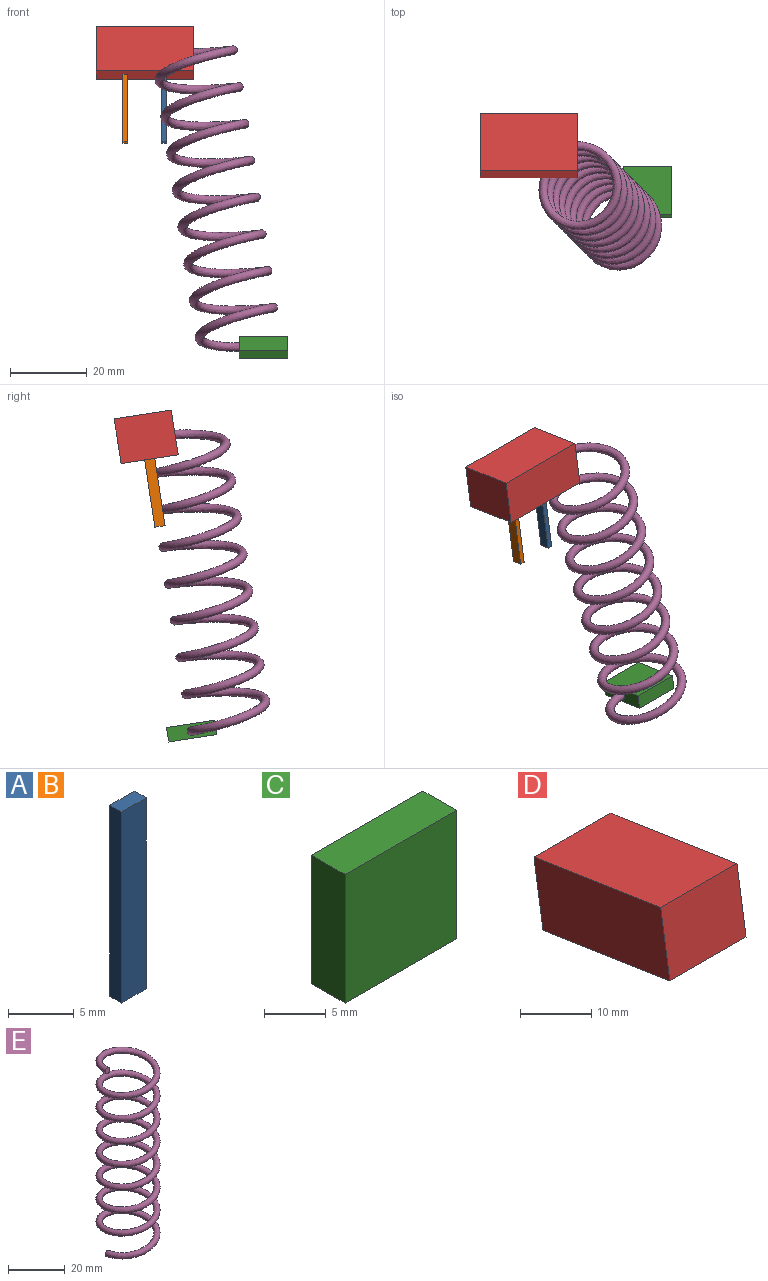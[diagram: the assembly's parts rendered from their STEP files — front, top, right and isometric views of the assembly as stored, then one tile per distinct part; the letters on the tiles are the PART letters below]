
ASSEMBLY  parts=5 mates=4
PART A: 6 faces, bbox 2.7x1.3x17.8 mm
  f0: plane 17.78x1.27mm, normal (-1,0,0), area 22.6mm2, adj f1,f3,f4,f5
  f1: plane 2.68x1.27mm, normal (0,0,-1), area 3.4mm2, adj f0,f2,f4,f5
  f2: plane 17.78x1.27mm, normal (1,0,0), area 22.6mm2, adj f1,f3,f4,f5
  f3: plane 2.68x1.27mm, normal (0,0,1), area 3.4mm2, adj f0,f2,f4,f5
  f4: plane 17.78x2.68mm, normal (0,-1,0), area 47.6mm2, adj f0,f1,f2,f3
  f5: plane 17.78x2.68mm, normal (0,1,0), area 47.6mm2, adj f0,f1,f2,f3
PART B: same geometry as A
PART C: 6 faces, bbox 12.7x3.8x12.7 mm
  f0: plane 12.7x3.81mm, normal (-1,0,0), area 48.4mm2, adj f1,f3,f4,f5
  f1: plane 12.7x12.7mm, normal (0,-1,0), area 161.3mm2, adj f0,f2,f4,f5
  f2: plane 12.7x3.81mm, normal (1,0,0), area 48.4mm2, adj f1,f3,f4,f5
  f3: plane 12.7x12.7mm, normal (0,1,0), area 161.3mm2, adj f0,f2,f4,f5
  f4: plane 12.7x3.81mm, normal (0,0,1), area 48.4mm2, adj f0,f1,f2,f3
  f5: plane 12.7x3.81mm, normal (0,0,-1), area 48.4mm2, adj f0,f1,f2,f3
PART D: 6 faces, bbox 15.1x26.9x15.6 mm
  f0: plane 26.91x15.56mm, normal (1,0,0), area 300.4mm2, adj f2,f3,f4,f5
  f1: plane 26.91x15.56mm, normal (-1,0,0), area 300.4mm2, adj f2,f3,f4,f5
  f2: plane 25.1x15.09mm, normal (0,0.15,0.99), area 383.2mm2, adj f0,f1,f3,f4
  f3: plane 15.09x11.69mm, normal (0,0.99,-0.15), area 178.4mm2, adj f0,f1,f2,f5
  f4: plane 15.09x11.69mm, normal (0,-0.99,0.15), area 178.4mm2, adj f0,f1,f2,f5
  f5: plane 25.1x15.09mm, normal (0,-0.15,-0.99), area 383.2mm2, adj f0,f1,f3,f4
PART E: 3 faces, bbox 22.8x22.8x83.2 mm
  f0: plane 2.25x2.22mm, normal (0,-0.99,0.15), area 4mm2, adj f2
  f1: plane 2.25x2.22mm, normal (0,0.99,-0.15), area 4mm2, adj f2
  f2: bspline ~83.18x22.83mm, area 3647.5mm2, adj f0,f1
PLACE A rot(axis=(0.71,-0.71,0.05),173.8deg) t=(-63.43,-7.13,146.65)mm
PLACE B rot(axis=(0.71,-0.71,0.05),173.8deg) t=(-73.59,-7.13,146.65)mm
PLACE C rot(axis=(-1,0,0),98.8deg) t=(24.69,28.6,59.98)mm
PLACE D rot(axis=(0,-0.15,-0.99),90deg) t=(-129.63,22.93,112.56)mm
PLACE E rot(axis=(-0.71,0.7,-0.11),180deg) t=(-6.12,24.81,124.76)mm
MATE fastened B.f1 <-> D.f5  axis (0,0.15,0.99) through (-72.96,42.49,108.39)mm
MATE fastened E.f0 <-> C.f0  axis (1,0,0) through (-43.17,31.53,37.33)mm
MATE fastened A.f1 <-> D.f5  axis (0,0.15,0.99) through (-62.8,42.49,108.39)mm
MATE fastened D.f3 <-> E.f1  axis (1,0,0) through (-55.18,43.39,114.24)mm
